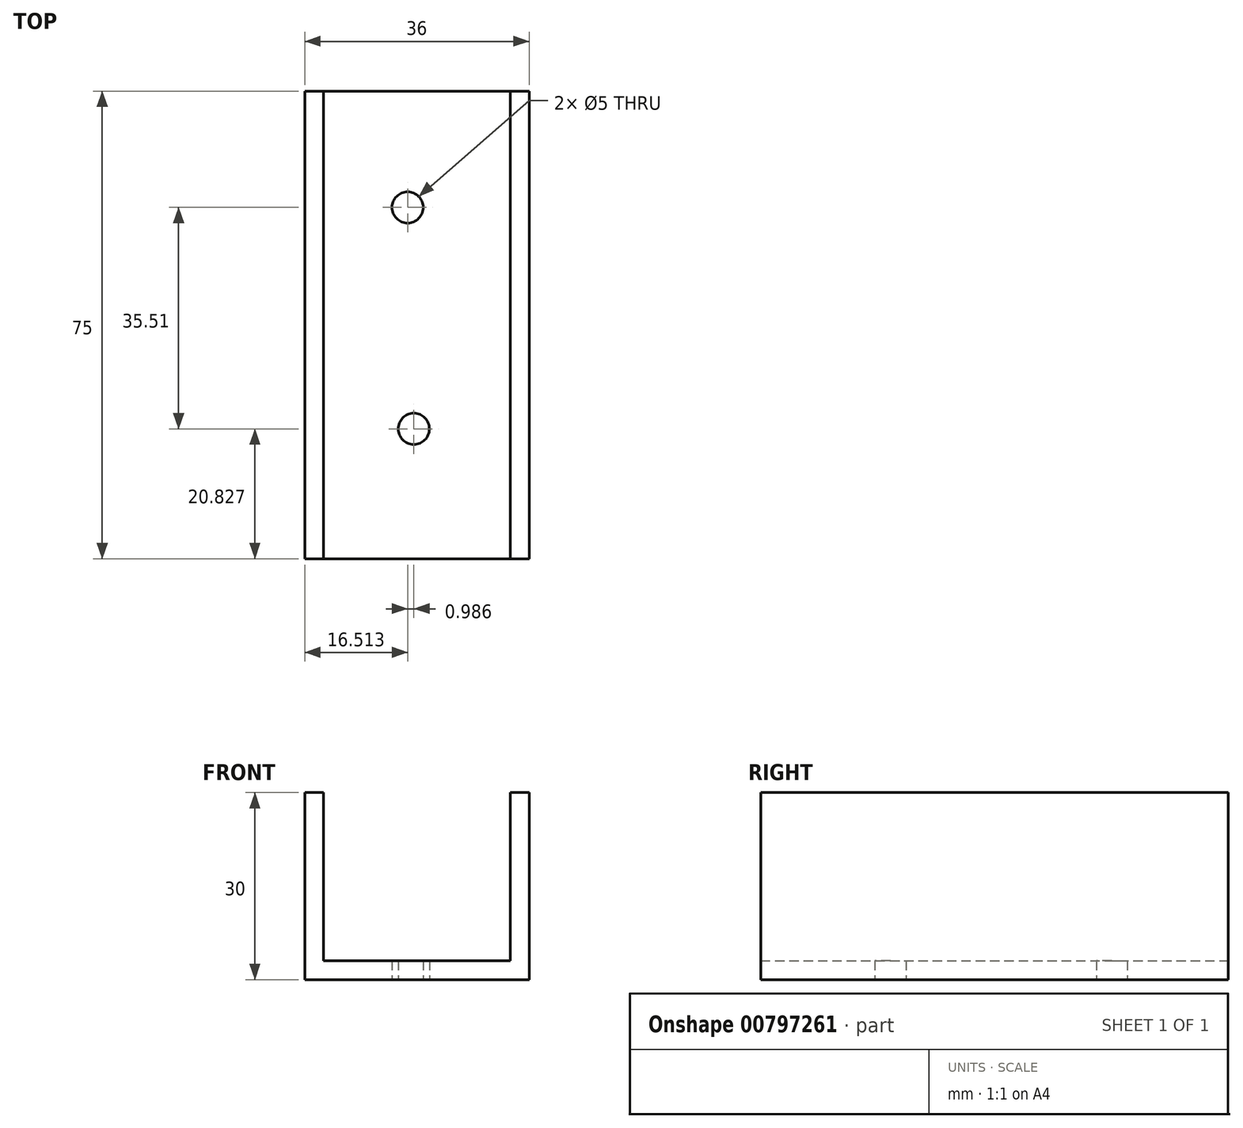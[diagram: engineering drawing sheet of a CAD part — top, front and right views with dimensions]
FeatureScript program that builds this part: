
annotation { "Feature Type Name" : "Feature", "Feature Type Description" : "" }
export const myFeature = defineFeature(function(context is Context, id is Id, definition is map)
    precondition{}
    {
        {
            var Q0;
            Q0=qCreatedBy(makeId("Top.planeOp"),FACE);
            var sketch = newSketch(context, id + "F0", { "sketchPlane" : qUnion([Q0])});
            skLineSegment(sketch, "E0.bottom", {"start": v(0, 0) * mm, "end": v(36, 0) * mm});
            skLineSegment(sketch, "E0.top", {"start": v(0, 75) * mm, "end": v(36, 75) * mm});
            skLineSegment(sketch, "E0.left", {"start": v(0, 0) * mm, "end": v(0, 75) * mm});
            skLineSegment(sketch, "E0.right", {"start": v(36, 0) * mm, "end": v(36, 75) * mm});
            skSolve(sketch);
        }
        {
            var Q0;
            Q0 = qSketchRegion(id + "F0", true);
            extrude(context, id + "F1", {"entities" : qUnion([Q0]), "depth" : 30 * mm, "offsetDistance" : 25 * mm});
        }
        {
            var Q0;
            Q0=makeQuery(id+"F1.opExtrude","SWEPT_FACE",FACE,{"disambiguationData":[OSD([sQuery(id+"F0.wireOp",EDGE,"E0.bottom")])]});
            var Q1;
            Q1=makeQuery(id+"F1.opExtrude","CAP_FACE",FACE,{"disambiguationData":[OSD([sQuery(id+"F0.wireOp",EDGE,"E0.bottom"),sQuery(id+"F0.wireOp",EDGE,"E0.top"),sQuery(id+"F0.wireOp",EDGE,"E0.left"),sQuery(id+"F0.wireOp",EDGE,"E0.right")])],"isStart":false});
            var Q2;
            Q2=makeQuery(id+"F1.opExtrude","SWEPT_FACE",FACE,{"disambiguationData":[OSD([sQuery(id+"F0.wireOp",EDGE,"E0.top")])]});
            shell(context, id + "F2", {"entities" : qUnion([Q0, Q1, Q2]), "thickness" : 3 * mm});
        }
        {
            var Q0;
            Q0=qCreatedBy(makeId("Top.planeOp"),FACE);
            var sketch = newSketch(context, id + "F3", { "sketchPlane" : qUnion([Q0])});
            skCircle(sketch, "E1", {"center": v(17.5, 20.83) * mm, "radius": 1.23 * mm});
            skCircle(sketch, "E2", {"center": v(16.51, 56.34) * mm, "radius": 1.5 * mm});
            skSolve(sketch);
        }
        {
            var Q0;
            Q0=sQuery(id+"F3.wireOp",VERTEX,"E1.center");
            var Q1;
            Q1=sQuery(id+"F3.wireOp",VERTEX,"E2.center");
            var Q2;
            Q2=makeQuery(id+"F1.opExtrude","SWEPT_BODY",BODY,{"disambiguationData":[OSD([sQuery(id+"F0.wireOp",EDGE,"E0.bottom"),sQuery(id+"F0.wireOp",EDGE,"E0.top"),sQuery(id+"F0.wireOp",EDGE,"E0.left"),sQuery(id+"F0.wireOp",EDGE,"E0.right")])]});
            hole(context, id + "F4", {"style" : HoleStyle.SIMPLE, "endStyle" : HoleEndStyle.THROUGH, "oppositeDirection" : true, "holeDiameter" : 5 * mm, "majorDiameter" : 5 * mm, "isTappedThrough" : true, "tappedDepth" : 12 * mm, "tapClearance" : 3, "locations" : qUnion([Q0, Q1]), "scope" : qUnion([Q2])});
        }
    });
